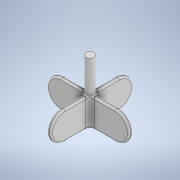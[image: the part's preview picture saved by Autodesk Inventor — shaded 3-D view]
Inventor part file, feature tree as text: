
AUTODESK INVENTOR PART (.ipt)
format: ipt  version: 2022 (Build 260153000, 153)  size: 279,552 bytes
history: native  units: mm
features: sketch x5, extrude x4, fillet x4
ambient origin geometry x8: Origin, YZ Plane, XZ Plane, XY Plane, X Axis, Y Axis, Z Axis, Center Point
bodies: Solid1 (feature_tree)
feature tree (13):
  extrude  "Extrusion1"  Depth=5.0mm
  sketch  "Sketch2"  dims[d2=5.0mm d3=66.0mm]
  extrude  "Extrusion2"  Depth=66.0mm
  extrude  "Extrusion3"  Depth=5.0mm TaperAngle=0.0deg
  extrude  "Extrusion4"  Depth=10.0mm
  fillet  "Fillet1"  Radius=40.0mm
  fillet  "Fillet2"  Radius=5.0mm
  fillet  "Fillet3"  Radius=5.0mm
  fillet  "Fillet4"  Radius=2.0mm
  sketch  "Sketch1"  dims[d0=66.0mm d1=5.0mm]
  sketch  "Sketch3"  dims[d4=34.0mm d5=0.0mm d6=5.0mm d7=0.0mm]
  sketch  "Sketch4"  dims[d8=5.0mm d9=0.0mm d10=10.0mm d11=40.0mm d12=0.0mm d13=5.0mm d14=5.0mm d15=2.0mm]
  sketch  "Sketch5"  dims[d16=2.0mm]
